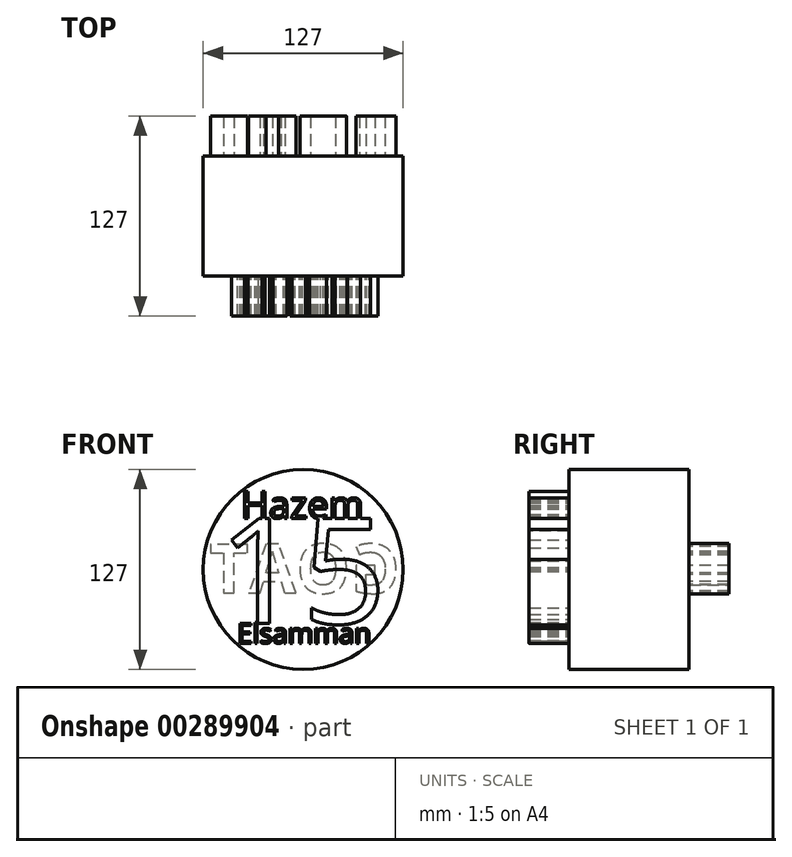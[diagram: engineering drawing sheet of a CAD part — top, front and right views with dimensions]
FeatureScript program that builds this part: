
annotation { "Feature Type Name" : "Feature", "Feature Type Description" : "" }
export const myFeature = defineFeature(function(context is Context, id is Id, definition is map)
    precondition{}
    {
        {
            var Q0;
            Q0=qCreatedBy(makeId("Front.planeOp"),FACE);
            var sketch = newSketch(context, id + "F0", { "sketchPlane" : qUnion([Q0])});
            skCircle(sketch, "E0", {"center": v(0, 0) * mm, "radius": 63.5 * mm});
            skSolve(sketch);
        }
        {
            var Q0;
            Q0 = qSketchRegion(id + "F0", true);
            extrude(context, id + "F1", {"entities" : qUnion([Q0]), "depth" : 76.2 * mm});
        }
        {
            var Q0;
            Q0=makeQuery(id+"F1.opExtrude","CAP_FACE",FACE,{"disambiguationData":[OSD([sQuery(id+"F0.wireOp",EDGE,"E0")])],"isStart":false});
            var sketch = newSketch(context, id + "F2", { "sketchPlane" : qUnion([Q0])});
            skText(sketch, "E1", { "text": "15\n", "fontName": "OpenSans-Regular.ttf"});
            const initialGuessF2  = {"E1": [-0.05421, -0.03429, 1, 0, 0.06736]};
            skSetInitialGuess(sketch, initialGuessF2);
            skSolve(sketch);
        }
        {
            var Q0;
            Q0 = qSketchRegion(id + "F2", true);
            extrude(context, id + "F3", {"entities" : qUnion([Q0]), "operationType" : NewBodyOperationType.ADD, "depth" : 25.4 * mm});
        }
        {
            var Q0;
            Q0=makeQuery(id+"F1.opExtrude","CAP_FACE",FACE,{"disambiguationData":[OSD([sQuery(id+"F0.wireOp",EDGE,"E0")])],"isStart":false});
            var sketch = newSketch(context, id + "F4", { "sketchPlane" : qUnion([Q0])});
            skText(sketch, "E2", { "text": "Hazem", "fontName": "OpenSans-Regular.ttf"});
            const initialGuessF4  = {"E2": [-0.03948, 0.0325, 1, 0, 0.01724]};
            skSetInitialGuess(sketch, initialGuessF4);
            skSolve(sketch);
        }
        {
            var Q0;
            Q0 = qSketchRegion(id + "F4", true);
            extrude(context, id + "F5", {"entities" : qUnion([Q0]), "operationType" : NewBodyOperationType.ADD, "depth" : 25.4 * mm});
        }
        {
            var Q0;
            {var subQ0=sQuery(id+"F0.wireOp",EDGE,"E0");Q0=makeQuery(id+"F5.boolean.opBoolean","SPLIT",FACE,{"disambiguationData":[TD([makeQuery(id+"F1.opExtrude","SWEPT_FACE",FACE,{"disambiguationData":[OSD([subQ0])]})])],"derivedFrom":makeQuery(id+"F1.opExtrude","CAP_FACE",FACE,{"disambiguationData":[OSD([subQ0])],"isStart":false})});}
            var sketch = newSketch(context, id + "F6", { "sketchPlane" : qUnion([Q0])});
            skText(sketch, "E3", { "text": "Elsamman\n", "fontName": "OpenSans-Regular.ttf"});
            const initialGuessF6  = {"E3": [-0.04197, -0.04686, 1, 0, 0.01257]};
            skSetInitialGuess(sketch, initialGuessF6);
            skSolve(sketch);
        }
        {
            var Q0;
            Q0 = qSketchRegion(id + "F6", true);
            extrude(context, id + "F7", {"entities" : qUnion([Q0]), "operationType" : NewBodyOperationType.ADD, "depth" : 25.4 * mm});
        }
        {
            var Q0;
            Q0=makeQuery(id+"F1.opExtrude","CAP_FACE",FACE,{"disambiguationData":[OSD([sQuery(id+"F0.wireOp",EDGE,"E0")])],"isStart":true});
            var sketch = newSketch(context, id + "F8", { "sketchPlane" : qUnion([Q0])});
            skText(sketch, "E4", { "text": "GOAT", "fontName": "OpenSans-Bold.ttf"});
            const initialGuessF8  = {"E4": [-0.06138, -0.01499, 1, 0, 0.03127]};
            skSetInitialGuess(sketch, initialGuessF8);
            skSolve(sketch);
        }
        {
            var Q0;
            Q0 = qSketchRegion(id + "F8", true);
            extrude(context, id + "F9", {"entities" : qUnion([Q0]), "operationType" : NewBodyOperationType.ADD, "depth" : 25.4 * mm});
        }
    });
